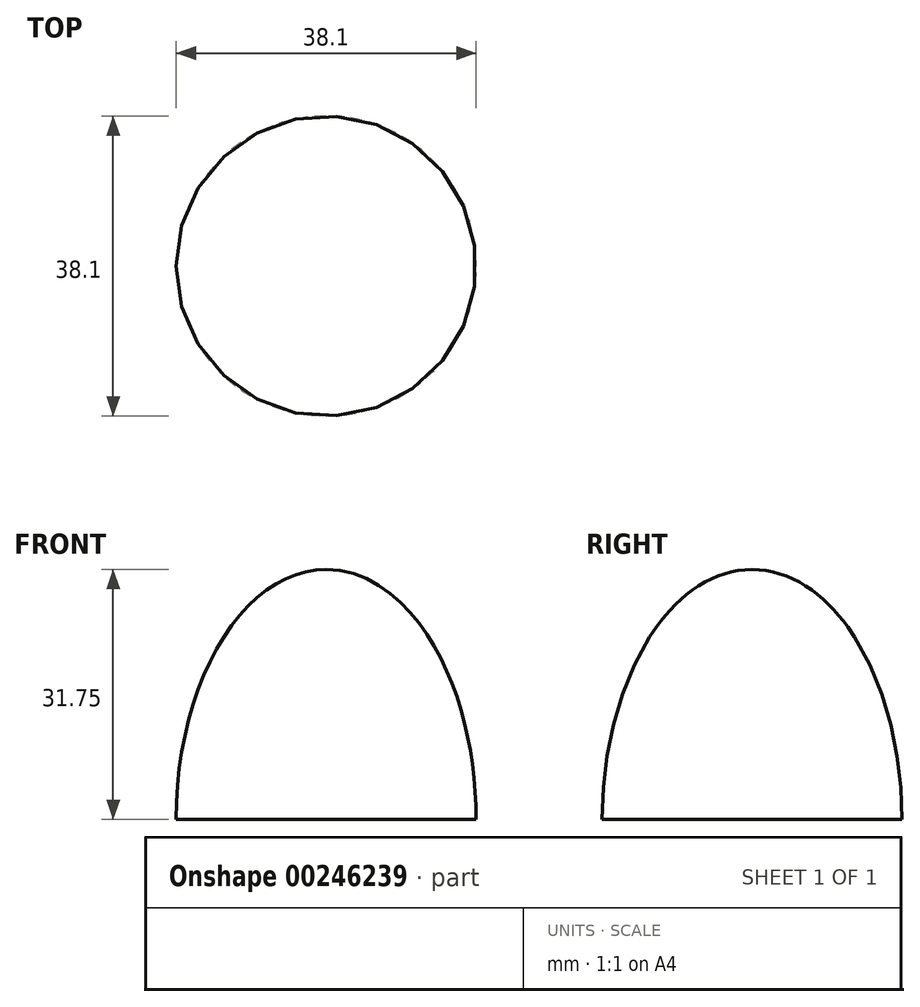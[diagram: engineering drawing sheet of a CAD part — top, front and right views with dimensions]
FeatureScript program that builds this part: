
annotation { "Feature Type Name" : "Feature", "Feature Type Description" : "" }
export const myFeature = defineFeature(function(context is Context, id is Id, definition is map)
    precondition{}
    {
        {
            var Q0;
            Q0=qCreatedBy(makeId("Front.planeOp"),FACE);
            var sketch = newSketch(context, id + "F0", { "sketchPlane" : qUnion([Q0])});
            skEllipticalArc(sketch, "E0", {});
            skLineSegment(sketch, "E1", {"start": v(-19.05, 0) * mm, "end": v(19.05, 0) * mm});
            skLineSegment(sketch, "E2", {"start": v(0, 0) * mm, "end": v(0, 44.63) * mm});
            const initialGuessF0  = {"E0": [0, 0, 0, 1, 0.03175, 0.01905, 4.71238898038469, 1.5707963267948966]};
            skSetInitialGuess(sketch, initialGuessF0);
            skSolve(sketch);
        }
        {
            var Q0;
            {var subQ0=sQuery(id+"F0.wireOp",EDGE,"E2");var subQ1=sQuery(id+"F0.wireOp",EDGE,"E0");var subQ2=makeQuery(id+"F0.imprint","INTERSECT",VERTEX,{"derivedFrom":[subQ1,subQ0]});Q0=makeQuery(id+"F0.imprint","IMPRINT",FACE,{"disambiguationData":[TD([[makeQuery(id+"F0.imprint","IMPRINT",EDGE,{"disambiguationData":[TD([[subQ2,-1.0]])],"derivedFrom":subQ1}),1.0]])]});}
            var Q1;
            Q1=sQuery(id+"F0.wireOp",EDGE,"E2");
            revolve(context, id + "F1", {"entities" : qUnion([Q0]), "axis" : qUnion([Q1]), "revolveType" : RevolveType.FULL});
        }
    });
